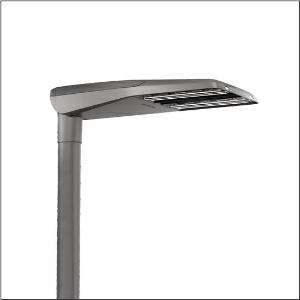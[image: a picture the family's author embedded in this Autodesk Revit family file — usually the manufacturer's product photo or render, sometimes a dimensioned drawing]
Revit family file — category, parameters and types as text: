
# Revit family: streetlight_sl_11_iq_midi___st1_2a_5xc3a41f08me_055e
name_source: partatom
category: Lighting Fixtures
units: mm (PartAtom-declared; Revit-internal decimal feet)

## family parameters
Cut with Voids When Loaded = No
Host = Face
Light Source = No
Part Type = Normal
Room Calculation Point = No
Round Connector Dimension = Use Diameter
Shared = No

## types (1)
- --- (1 x LED, 18900 lm, 124.7 W, 4000K)
    Apparent Load = 125 VA
    CIE Flux Codes = 32 70 96 100 100
    Color Rendering = 70
    Color Temperature = 4000K
    Default Elevation = 1800 mm
    Description = Streetlight SL 11 iQ midi, mast luminaire, primary light control with 3 zone facetted reflector, of plastic, silver coated, highly specular, primary optical cover: cover, of PMMA, transparent, light distribution: ST1.2a, light emission: direct distribution, primary light characteristic: asymmetric, installation type: post-top, side-entry, LED, High Power LED, rated luminous flux: 18.900lm, luminous efficacy: 152lm/W, light colour: 740, colour temperature: 4000K, control: Street-Remote, optimised constant luminous flux control (CLO 2.0), Desk-Remote (wireless, voltage-free reading and setting of iQ features in the workshop via application-optimized NFC function/RFID function), Light-Fading, Smart-Wire, Night-Set, Lumen-Switch, Temp-Guard, Auto-Match, with cable H07RN-F 5x 1.5mm², mains connection: 230..240V, AC, 50/60Hz, connection cable pre-assembled, cable length: 12,5m, start of lifetime: 125W, end of service life: 132W, reduction: 57W, luminaire housing, of diecast aluminium, powder-coated, Siteco® metallic grey (DB 702S), please order mast flange separately, inclination adjustable without tools: 0°, 5°, 10°, 15° (post-top) | 0°, -5°, -10°, -15° (side-entry), sealing non-destructively replaceable, multi-level sealing system, length: 780mm, width: 376mm, height: 118mm, mast flange for spigot size: 42mm (side-entry): 5XC10008XM4, 60/48mm (side-entry/post-top): 5XC10108XM2, 76/60mm (side-entry/post-top): 5XC10108XM1, equipment: Power, protection rating (complete): IP66, insulation class (complete): insulation class II (safety insulation), certification: CE, ENEC, VDE, impact resistance: IK09, permissible operating ambient temperature for outdoor applications: -25..+50°C, standard-compliant lighting for roads and squares, Environmental Product Declaration (EPD) tested and certified by an independent institute, packaging unit: 1 piece

Light Distribution: ST1.2a
    Height = 118 mm
    Lamp = 1 x LED
    Lamp Light Flux = 18900 lm
    Lamp Power = 124.7 W
    Lamp count = 1
    Length = 780 mm
    Luminous efficacy = 152 lm/W
    Manufacturer = Siteco
    ModVariant = No
    Model = 5XC3A41F08ME
    Number of Poles = 1
    OnlyDefault = Yes
    Power Factor = 1
    Product Name = Streetlight SL 11 iQ midi | ST1.2a
    Product group = mast luminaire | pylon top
    ProductGroupID = 6100
    Protection Class = Protection class II
    Protection Degree = IP 66
    RLX_Detail_Level = 1
    RLX_Emergency_Light_Flux = 0 lm
    RLX_Emergency_Type = 0
    RLX_Emergency_Type_DB = No
    RlxData = <blob elided: 70845 chars, md5=f72629a9>
    Socket = socket
    Standby Power = 0 W
    System Light Flux = 18900 lm
    System Power = 125 W
    Type Comments = factory setting: luminous flux: 100 % | dim-lin: 254 | 557 mA
    Type Image = l_1005960.jpg
    URL = http://relux.com
    VarID = @adj_149779
    Voltage = 0 V
    Weight = 0.00 kg
    Width = 376 mm

## geometry (parser evidence)
native form markers: Blend x4, Sweep x9
no freeform markers — native parametric forms only
